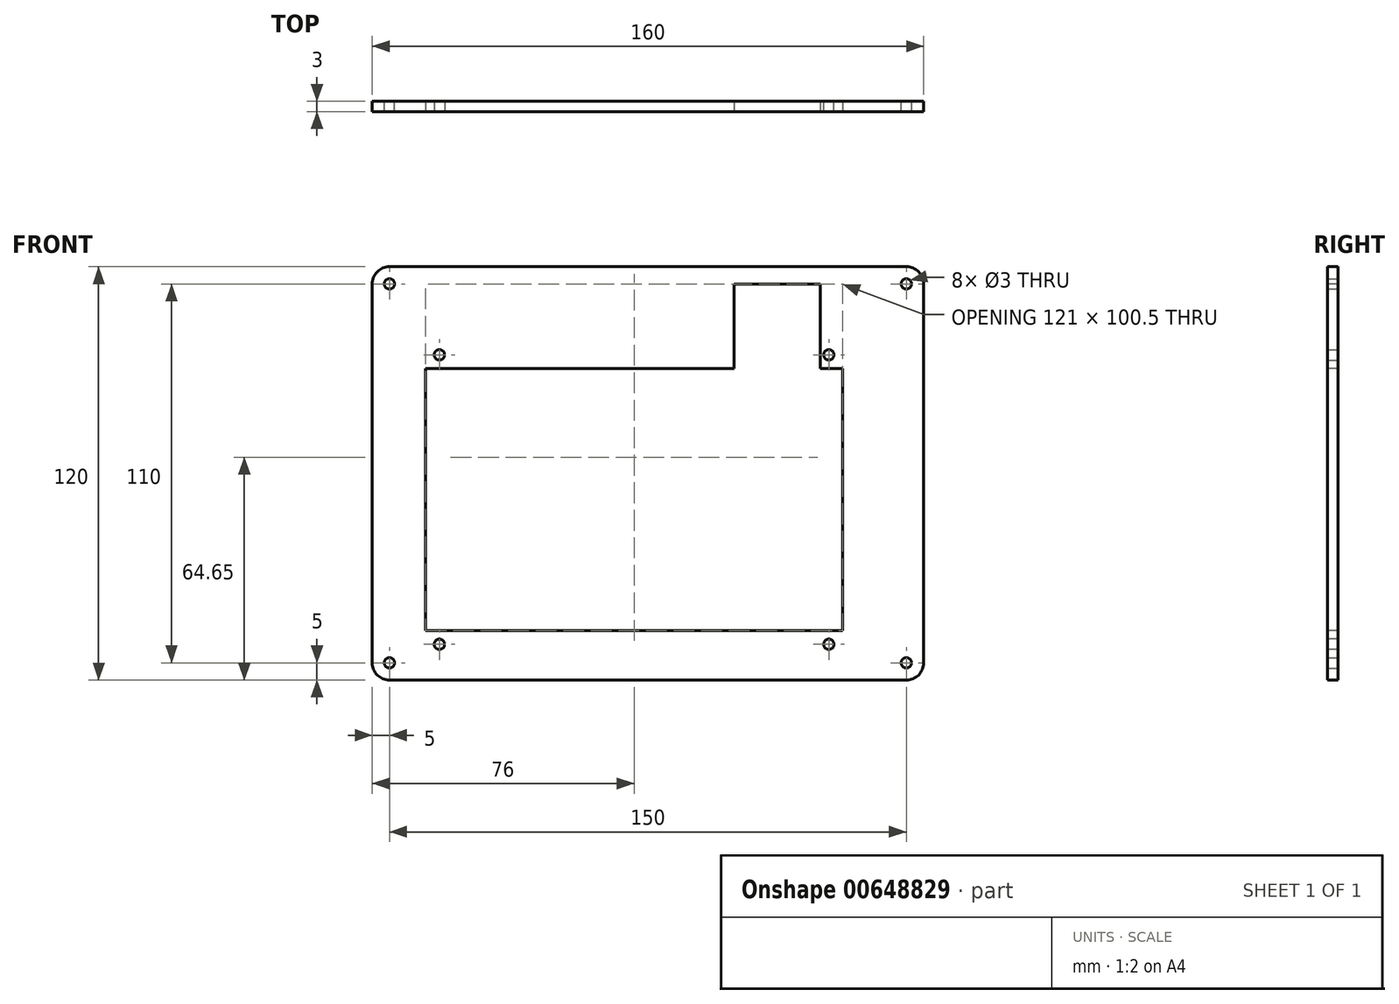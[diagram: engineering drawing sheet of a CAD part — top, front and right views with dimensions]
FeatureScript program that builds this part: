
annotation { "Feature Type Name" : "Feature", "Feature Type Description" : "" }
export const myFeature = defineFeature(function(context is Context, id is Id, definition is map)
    precondition{}
    {
        {
            var Q0;
            Q0=qCreatedBy(makeId("Front.planeOp"),FACE);
            var sketch = newSketch(context, id + "F0", { "sketchPlane" : qUnion([Q0])});
            skLineSegment(sketch, "E0.bottom", {"start": v(75, -60) * mm, "end": v(-75, -60) * mm});
            skLineSegment(sketch, "E0.top", {"start": v(75, 60) * mm, "end": v(-75, 60) * mm});
            skLineSegment(sketch, "E0.left", {"start": v(80, -55) * mm, "end": v(80, 55) * mm});
            skLineSegment(sketch, "E0.right", {"start": v(-80, -55) * mm, "end": v(-80, 55) * mm});
            skPoint(sketch, "E0.middle", {"position": v(0, 0) * mm});
            skPoint(sketch, "E1.visualSharp", {"position": v(-80, 60) * mm});
            skArc(sketch, "E1.filletArc", {"start": v(-75, 60) * mm, "mid": v(-78.54, 58.54) * mm, "end": v(-80, 55) * mm});
            skPoint(sketch, "E2.visualSharp", {"position": v(80, 60) * mm});
            skArc(sketch, "E2.filletArc", {"start": v(80, 55) * mm, "mid": v(78.54, 58.54) * mm, "end": v(75, 60) * mm});
            skPoint(sketch, "E3.visualSharp", {"position": v(80, -60) * mm});
            skArc(sketch, "E3.filletArc", {"start": v(75, -60) * mm, "mid": v(78.54, -58.54) * mm, "end": v(80, -55) * mm});
            skPoint(sketch, "E4.visualSharp", {"position": v(-80, -60) * mm});
            skArc(sketch, "E4.filletArc", {"start": v(-80, -55) * mm, "mid": v(-78.54, -58.54) * mm, "end": v(-75, -60) * mm});
            skSolve(sketch);
        }
        {
            var Q0;
            Q0=makeQuery(id+"F0.imprint","IMPRINT",FACE,{"disambiguationData":[TD([[makeQuery(id+"F0.imprint","IMPRINT",EDGE,{"derivedFrom":sQuery(id+"F0.wireOp",EDGE,"E0.bottom")}),-1.0]])]});
            extrude(context, id + "F1", {"entities" : qUnion([Q0]), "depth" : 3 * mm, "offsetDistance" : 25 * mm});
        }
        {
            var Q0;
            Q0=qCreatedBy(makeId("Front.planeOp"),FACE);
            var sketch = newSketch(context, id + "F2", { "sketchPlane" : qUnion([Q0])});
            skCircle(sketch, "E5", {"center": v(-75, 55) * mm, "radius": 1.5 * mm});
            skCircle(sketch, "E6", {"center": v(75, 55) * mm, "radius": 1.5 * mm});
            skCircle(sketch, "E7", {"center": v(75, -55) * mm, "radius": 1.5 * mm});
            skCircle(sketch, "E8", {"center": v(-75, -55) * mm, "radius": 1.5 * mm});
            skSolve(sketch);
        }
        {
            var Q0;
            Q0=qSketchRegion(id+"F2",true);
            extrude(context, id + "F3", {"entities" : qUnion([Q0]), "operationType" : NewBodyOperationType.REMOVE, "depth" : 25 * mm, "offsetDistance" : 25 * mm});
        }
        {
            var Q0;
            Q0=qCreatedBy(makeId("Front.planeOp"),FACE);
            var sketch = newSketch(context, id + "F4", { "sketchPlane" : qUnion([Q0])});
            skPoint(sketch, "E9.start.orphan", {"position": v(0, -27.1) * mm});
            skCircle(sketch, "E10", {"center": v(52.5, 34.4) * mm, "radius": 1.5 * mm});
            skSolve(sketch);
        }
        {
            var Q0;
            Q0=makeQuery(id+"F4.imprint","IMPRINT",FACE,{"disambiguationData":[TD([[makeQuery(id+"F4.imprint","IMPRINT",EDGE,{"derivedFrom":sQuery(id+"F4.wireOp",EDGE,"3Q8pNaT9-MZu4-fZL0-JBpA-oB1KTClbxi4n")}),1.0]])]});
            var Q1;
            Q1=makeQuery(id+"F4.imprint","IMPRINT",FACE,{"disambiguationData":[TD([[makeQuery(id+"F4.imprint","IMPRINT",EDGE,{"derivedFrom":sQuery(id+"F4.wireOp",EDGE,"E10")}),1.0]])]});
            var Q2;
            Q2=makeQuery(id+"F4.imprint","IMPRINT",FACE,{"disambiguationData":[TD([[makeQuery(id+"F4.imprint","IMPRINT",EDGE,{"derivedFrom":sQuery(id+"F4.wireOp",EDGE,"r2QVgMR1-3B4m-qnwO-mz9k-peFpHc5iAmY2")}),1.0]])]});
            var Q3;
            Q3=makeQuery(id+"F4.imprint","IMPRINT",FACE,{"disambiguationData":[TD([[makeQuery(id+"F4.imprint","IMPRINT",EDGE,{"derivedFrom":sQuery(id+"F4.wireOp",EDGE,"o2jHBMil-3RIS-sA2l-7ex4-zNIZPRWduCML")}),1.0]])]});
            extrude(context, id + "F5", {"entities" : qUnion([Q0, Q1, Q2, Q3]), "operationType" : NewBodyOperationType.REMOVE, "depth" : 25 * mm, "offsetDistance" : 25 * mm});
        }
        {
            var Q0;
            Q0=makeQuery(id+"F1.opExtrude","CAP_FACE",FACE,{"disambiguationData":[OSD([sQuery(id+"F0.wireOp",EDGE,"E0.bottom"),sQuery(id+"F0.wireOp",EDGE,"E0.top"),sQuery(id+"F0.wireOp",EDGE,"E0.left"),sQuery(id+"F0.wireOp",EDGE,"E0.right"),sQuery(id+"F0.wireOp",EDGE,"E1.filletArc"),sQuery(id+"F0.wireOp",EDGE,"E2.filletArc"),sQuery(id+"F0.wireOp",EDGE,"E3.filletArc"),sQuery(id+"F0.wireOp",EDGE,"E4.filletArc")])],"isStart":false});
            var sketch = newSketch(context, id + "F6", { "sketchPlane" : qUnion([Q0])});
            skLineSegment(sketch, "E11", {"start": v(-64.5, 30.4) * mm, "end": v(56.5, 30.4) * mm});
            skCircle(sketch, "E12.0", {"center": v(52.5, 34.4) * mm, "radius": 1.5 * mm});
            skCircle(sketch, "E13", {"center": v(-60.5, 34.4) * mm, "radius": 1.5 * mm});
            skCircle(sketch, "E14", {"center": v(-60.5, -49.6) * mm, "radius": 1.5 * mm});
            skCircle(sketch, "E15", {"center": v(52.5, -49.6) * mm, "radius": 1.5 * mm});
            skLineSegment(sketch, "E16", {"start": v(-64.5, -45.6) * mm, "end": v(56.5, -45.6) * mm});
            skLineSegment(sketch, "E17", {"start": v(-64.5, 30.4) * mm, "end": v(-64.5, -45.6) * mm});
            skLineSegment(sketch, "E18", {"start": v(56.5, 30.4) * mm, "end": v(56.5, -45.6) * mm});
            skSolve(sketch);
        }
        {
            var Q0;
            Q0=qSketchRegion(id+"F6",true);
            extrude(context, id + "F7", {"entities" : qUnion([Q0]), "operationType" : NewBodyOperationType.REMOVE, "oppositeDirection" : true, "depth" : 3 * mm, "offsetDistance" : 25 * mm});
        }
        {
            var Q0;
            Q0=makeQuery(id+"F1.opExtrude","CAP_FACE",FACE,{"disambiguationData":[OSD([sQuery(id+"F0.wireOp",EDGE,"E0.bottom"),sQuery(id+"F0.wireOp",EDGE,"E0.top"),sQuery(id+"F0.wireOp",EDGE,"E0.left"),sQuery(id+"F0.wireOp",EDGE,"E0.right"),sQuery(id+"F0.wireOp",EDGE,"E1.filletArc"),sQuery(id+"F0.wireOp",EDGE,"E2.filletArc"),sQuery(id+"F0.wireOp",EDGE,"E3.filletArc"),sQuery(id+"F0.wireOp",EDGE,"E4.filletArc")])],"isStart":false});
            var sketch = newSketch(context, id + "F8", { "sketchPlane" : qUnion([Q0])});
            skPoint(sketch, "E19.0.center.orphan", {"position": v(52.5, 34.4) * mm});
            skPoint(sketch, "E20.middle", {"position": v(37.5, 42.4) * mm});
            skLineSegment(sketch, "E21.bottom", {"start": v(50, 54.9) * mm, "end": v(25, 54.9) * mm});
            skLineSegment(sketch, "E21.top", {"start": v(50, 29.9) * mm, "end": v(25, 29.9) * mm});
            skLineSegment(sketch, "E21.left", {"start": v(50, 54.9) * mm, "end": v(50, 29.9) * mm});
            skLineSegment(sketch, "E21.right", {"start": v(25, 54.9) * mm, "end": v(25, 29.9) * mm});
            skSolve(sketch);
        }
        {
            var Q0;
            {var subQ0=sQuery(id+"F8.wireOp",EDGE,"E21.bottom");Q0=makeQuery(id+"F8.imprint","IMPRINT",FACE,{"disambiguationData":[TD([[makeQuery(id+"F8.imprint","IMPRINT",EDGE,{"derivedFrom":subQ0}),1.0]])]});}
            extrude(context, id + "F9", {"entities" : qUnion([Q0]), "operationType" : NewBodyOperationType.REMOVE, "oppositeDirection" : true, "depth" : 3 * mm, "offsetDistance" : 25 * mm});
        }
    });
